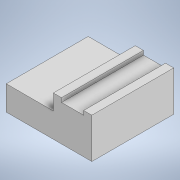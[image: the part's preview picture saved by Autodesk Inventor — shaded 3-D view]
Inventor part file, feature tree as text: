
AUTODESK INVENTOR PART (.ipt)
format: ipt  version: 2021 (Build 250183000, 183)  size: 116,736 bytes
history: native  units: mm
features: extrude x2, sketch x2
ambient origin geometry x8: Origin, YZ Plane, XZ Plane, XY Plane, X Axis, Y Axis, Z Axis, Center Point
bodies: Solid1 (feature_tree)
feature tree (4):
  extrude  "Extrusion1"  Depth=8.8mm
  extrude  "Extrusion2"  Depth=1.0mm
  sketch  "Sketch1"  dims[d0=13.5mm d1=8.8mm]
  sketch  "Sketch2"  dims[d2=5.4mm d3=1.0mm d4=2.0mm d5=6.0mm d6=20.0mm d7=0.0mm d8=3.0mm d9=14.0mm d10=2.8mm d11=7.0mm d12=10.0mm d13=0.0mm]
